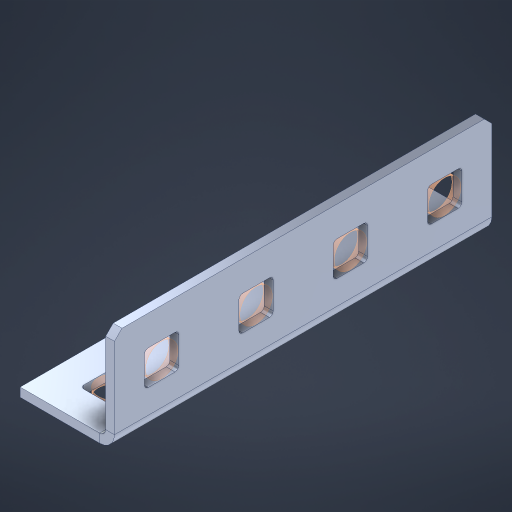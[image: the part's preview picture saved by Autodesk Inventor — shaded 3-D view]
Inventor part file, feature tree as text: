
AUTODESK INVENTOR PART (.ipt)
format: ipt  version: 2023 (Build 270158000, 158)  size: 419,840 bytes
history: native  units: in
note: dims shown in document units (in); Inventor stores cm internally (conversion verified against a paired STEP export)
features: other x13, sheet_metal_op x10, sketch x8, extrude x7, mirror x1, pattern_linear x1, chamfer x1
ambient origin geometry x8: Origin, YZ Plane, XZ Plane, XY Plane, X Axis, Y Axis, Z Axis, Center Point
bodies: Solid1 (feature_tree), Body (feature_tree)
feature tree (41):
  other  "Flange Pattern Plane"
  sheet_metal_op  "Flange Pattern"
  sheet_metal_op  "Body Pattern"
  other  "Arc Length"
  mirror  "Notch Mirror"
  pattern_linear  "Notch Pattern"  Spacing1=0.1875in  [1 undecoded]
  chamfer  "End Chamfer"
  extrude  "Half Cut"  Depth=0.0469in
  sketch  "Sketch1"  dims[d0=2.5in]
  other  "Plate1"
  sketch  "Sketch2"  dims[d1=2.0in]
  other  "Plate2"
  sheet_metal_op  "Bend1"
  sheet_metal_op  "Corner1"
  sketch  "Sketch3"  dims[d2=0.0469in]
  other  "Flange Pattern Sketch"
  sketch  "Sketch7"  dims[d3=0.0469in]
  other  "Srf1"
  other  "Srf2"
  sketch  "Sketch8"  dims[d4=0.0234in]
  sketch  "Sketch9"  dims[d5=0.0938in]
  other  "Srf91"
  sheet_metal_op  "Body Pattern Sketch"
  other  "Srf92"
  sketch  "Sketch13"  dims[d6=0.0469in]
  sketch  "Sketch14"  dims[d7=0.5in d8=90.0deg d9=0.0312in d10=0.1875in d11=0.0469in d12=0.0469in d16=0.182in d17=0.02in d18=0.0469in d19=0.0in d20=0.25in d21=0.25in d46=0.172in d47=1.0in d48=0.0in d49=0.182in d50=0.02in d51=0.25in d52=0.25in d53=0.0469in d54=0.0in d55=0.172in d56=1.0in d57=0.0in d60=1.5748in d62=0.5in d63=0.3937in d65=0.5in d85=0.1227in d86=0.1659in d88=0.04in d89=0.0469in d90=0.0in d91=0.04in d92=0.0491in d95=2.5in d96=0.04in d97=0.25in d98=45.0deg d101=0.0in d102=2.497in d131=0.5in d132=1.5748in d134=0.5in d139=0.5in]
  other  "Srf856"
  other  "Srf1310"
  other  "Srf1311"
  other  "Srf1376"
  sheet_metal_op  "Flange Stamp"
  sheet_metal_op  "Flange Circle"
  sheet_metal_op  "Body Stamp"
  sheet_metal_op  "Body Circle"
  sheet_metal_op  "Notch"
  extrude  "ExtrusionSrf2"  Depth=0.0469in
  extrude  "ExtrusionSrf92"  Depth=0.182in
  extrude  "ExtrusionSrf856"  Depth=0.02in
  extrude  "ExtrusionSrf1310"  Depth=0.0469in
  extrude  "ExtrusionSrf1311"  TaperAngle=0.0deg  [1 undecoded]
  extrude  "ExtrusionSrf1376"  Depth=0.5in
note: 2 required parameter values undecoded (feature->parameter linkage not recoverable at this tier; creation-order binding heuristic only, values carry confidence <= 0.55)
